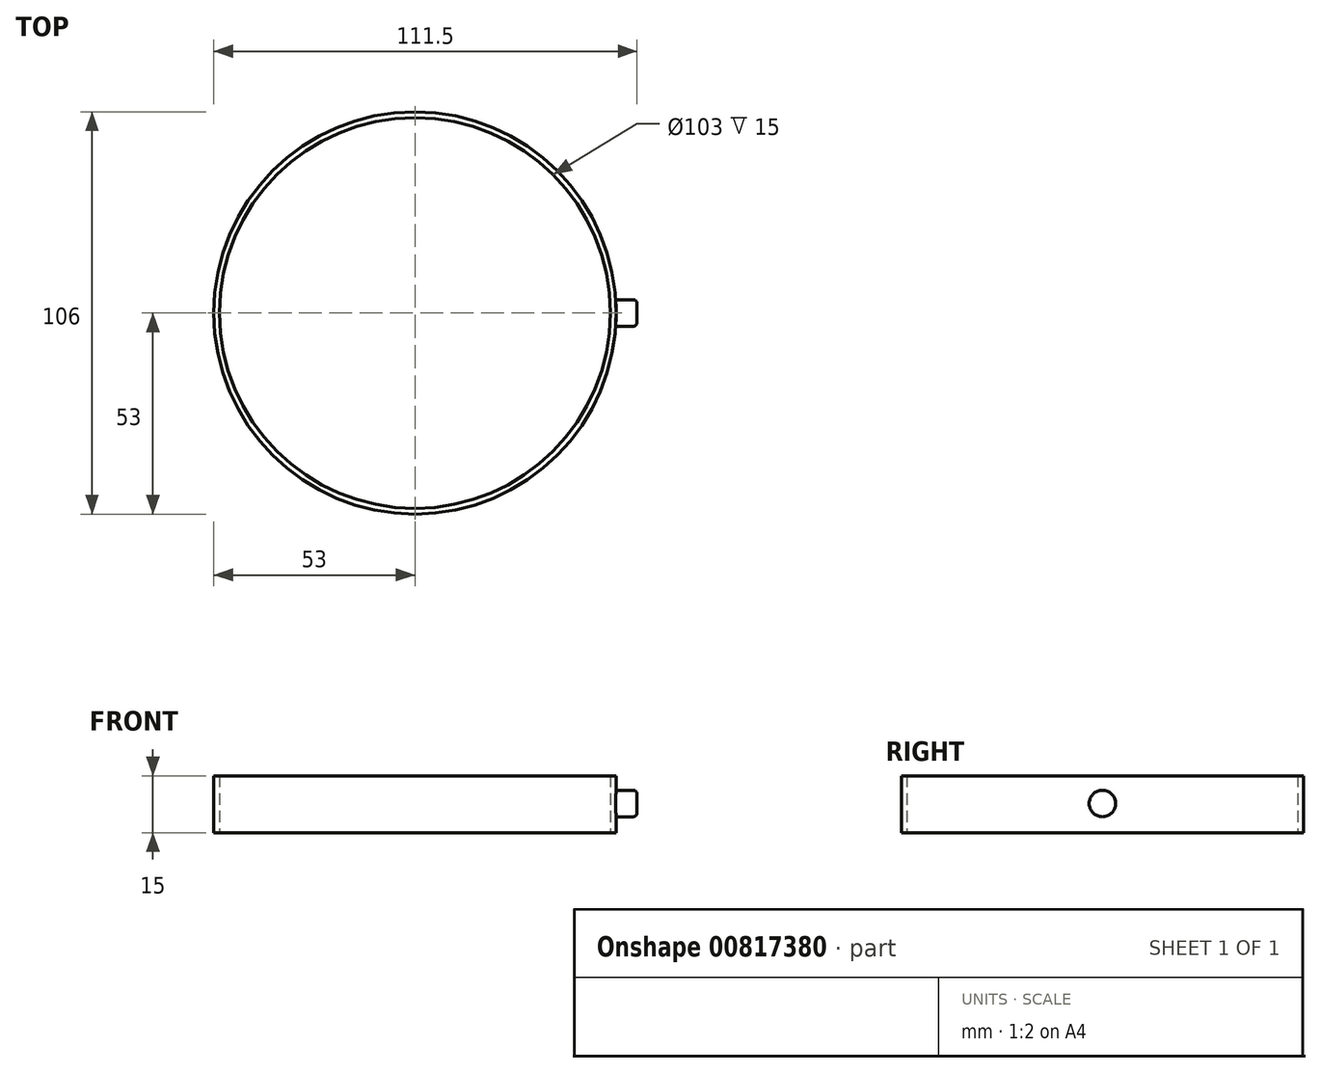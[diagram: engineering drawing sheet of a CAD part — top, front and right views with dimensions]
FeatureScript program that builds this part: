
annotation { "Feature Type Name" : "Feature", "Feature Type Description" : "" }
export const myFeature = defineFeature(function(context is Context, id is Id, definition is map)
    precondition{}
    {
        {
            var Q0;
            Q0=qCreatedBy(makeId("Top.planeOp"),FACE);
            var sketch = newSketch(context, id + "F0", { "sketchPlane" : qUnion([Q0])});
            skCircle(sketch, "E0", {"center": v(0, 0) * mm, "radius": 51.5 * mm});
            skCircle(sketch, "E1.0", {"center": v(0, 0) * mm, "radius": 53 * mm});
            skSolve(sketch);
        }
        {
            var Q0;
            Q0=makeQuery(id+"F0.imprint","IMPRINT",FACE,{"disambiguationData":[TD([[makeQuery(id+"F0.imprint","IMPRINT",EDGE,{"derivedFrom":sQuery(id+"F0.wireOp",EDGE,"E0")}),-1.0]])]});
            extrude(context, id + "F1", {"entities" : qUnion([Q0]), "depth" : 15 * mm, "offsetDistance" : 25 * mm});
        }
        {
            var Q0;
            Q0=qCreatedBy(makeId("Right.planeOp"),FACE);
            cPlane(context, id + "F2", {"entities" : qUnion([Q0]), "cplaneType" : CPlaneType.OFFSET, "offset" : 51.5 * mm, "width" : 150 * mm, "height" : 150 * mm});
        }
        {
            var Q0;
            Q0=qCreatedBy(id+"F2.planeOp",FACE);
            var sketch = newSketch(context, id + "F3", { "sketchPlane" : qUnion([Q0])});
            skCircle(sketch, "E2", {"center": v(0, 7.73) * mm, "radius": 3.5 * mm});
            skSolve(sketch);
        }
        {
            var Q0;
            Q0=qSketchRegion(id+"F3",true);
            extrude(context, id + "F4", {"entities" : qUnion([Q0]), "operationType" : NewBodyOperationType.ADD, "depth" : 7 * mm, "offsetDistance" : 25 * mm});
        }
        {
            var Q0;
            Q0=makeQuery(id+"F4.opExtrude","CAP_EDGE",EDGE,{"disambiguationData":[OSD([sQuery(id+"F3.wireOp",EDGE,"E2")])],"isStart":false});
            fillet(context, id + "F5", {"entities" : qUnion([Q0]), "radius" : 1 * mm, "tangentPropagation" : true, "allowEdgeOverflow" : false});
        }
    });
